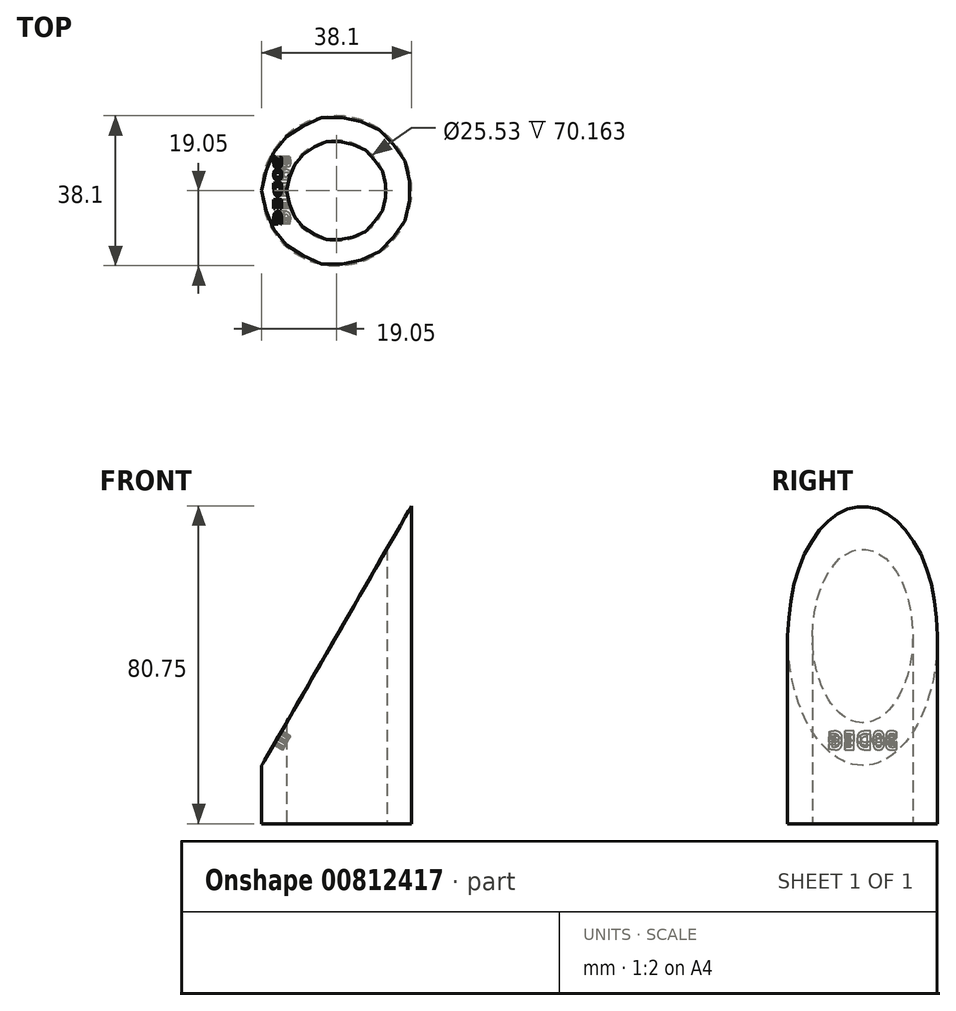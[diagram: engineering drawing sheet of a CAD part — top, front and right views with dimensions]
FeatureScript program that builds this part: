
annotation { "Feature Type Name" : "Feature", "Feature Type Description" : "" }
export const myFeature = defineFeature(function(context is Context, id is Id, definition is map)
    precondition{}
    {
        {
            var Q0;
            Q0=qCreatedBy(makeId("Top.planeOp"),FACE);
            var sketch = newSketch(context, id + "F0", { "sketchPlane" : qUnion([Q0])});
            skCircle(sketch, "E0", {"center": v(0, 0) * mm, "radius": 12.76 * mm});
            skCircle(sketch, "E1", {"center": v(0, 0) * mm, "radius": 19.05 * mm});
            skSolve(sketch);
        }
        {
            var Q0;
            Q0 = qSketchRegion(id + "F0", true);
            extrude(context, id + "F1", {"entities" : qUnion([Q0]), "depth" : 88.9 * mm, "offsetDistance" : 25.4 * mm});
        }
        {
            var Q0;
            Q0=qCreatedBy(makeId("Front.planeOp"),FACE);
            var sketch = newSketch(context, id + "F2", { "sketchPlane" : qUnion([Q0])});
            skLineSegment(sketch, "E2", {"start": v(35.96, 110.03) * mm, "end": v(-29.62, -3.55) * mm});
            skLineSegment(sketch, "E3", {"start": v(35.96, 110.03) * mm, "end": v(-33.17, 110.03) * mm});
            skLineSegment(sketch, "E4", {"start": v(-33.17, 110.03) * mm, "end": v(-29.62, -3.55) * mm});
            skSolve(sketch);
        }
        {
            var Q0;
            Q0 = qSketchRegion(id + "F2", true);
            extrude(context, id + "F3", {"entities" : qUnion([Q0]), "operationType" : NewBodyOperationType.REMOVE, "endBound" : BoundingType.SYMMETRIC, "oppositeDirection" : true, "depth" : 127 * mm, "offsetDistance" : 25.4 * mm});
        }
        {
            var Q0;
            Q0=makeQuery(id+"F3.boolean.opBoolean","COPY",FACE,{"derivedFrom":makeQuery(id+"F3.opExtrude","SWEPT_FACE",FACE,{"disambiguationData":[OSD([sQuery(id+"F2.wireOp",EDGE,"E2")])]})});
            var sketch = newSketch(context, id + "F4", { "sketchPlane" : qUnion([Q0])});
            skText(sketch, "E5", { "text": "30DEG", "fontName": "OpenSans-Bold.ttf"});
            const initialGuessF4  = {"E5": [-0.0089, 0.00936, 1, 0, 0.00406]};
            skSetInitialGuess(sketch, initialGuessF4);
            skSolve(sketch);
        }
        {
            var Q0;
            Q0 = qSketchRegion(id + "F4", true);
            extrude(context, id + "F5", {"entities" : qUnion([Q0]), "operationType" : NewBodyOperationType.REMOVE, "oppositeDirection" : true, "depth" : 2.54 * mm, "offsetDistance" : 25.4 * mm});
        }
    });
